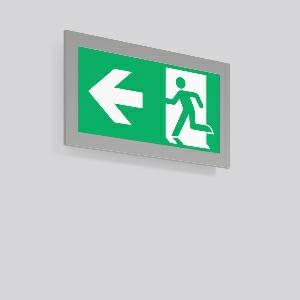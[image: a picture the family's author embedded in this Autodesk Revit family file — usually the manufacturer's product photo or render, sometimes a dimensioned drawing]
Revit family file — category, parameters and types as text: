
# Revit family: tenuo_671923_004_89_73a6
name_source: partatom
category: Lighting Fixtures
units: mm (PartAtom-declared; Revit-internal decimal feet)

## family parameters
Cut with Voids When Loaded = No
Host = Face
Light Source = No
Part Type = Normal
Room Calculation Point = No
Round Connector Dimension = Use Diameter
Shared = No

## types (1)
- TENUO
    Apparent Load = 0 VA
    Default Elevation = 1800 mm
    Description = Series: TENUO
Luminaire for escape route identification. Housing: anodised aluminium, silver. Display panel: patented MicroLens technology and legend on one side. Driver integrated. Suitable for connection to central battery systems. With AC Control monitoring module for LUXIFAIR central battery units. Please indicate legend number when placing your order! 
Colour: silver, matt (approx. RAL 9006)
Length: 350 mm
Width: 33 mm
Height: 200 mm
Weight: 1.52 kg
Operating mode: maintained power mode
Viewing Distance: 30 m
Lamp: LED
Socket: without socket
Colour temperature: 5700K
Colour rendering index (CRI): 80
System power: 4.8 W
System power, emergency: 4.8 W
Control gear: Regulated power supply
Protection class: I
Type of protection: IP 40
    Height = 200 mm  [stored 0.656168 ft]
    Lamp = 0 x
    Length = 350 mm
    Luminous efficacy = 0 lm/W
    Manufacturer = RZB
    ModVariant = No
    Model = 671923.004.89
    Mounting Place = Wall
    Mounting Type = Surface mounted
    Number of Poles = 1
    OnlyDefault = Yes
    Power Factor = 1
    Product Name = TENUO
    Product group = Surface mounted Wall luminaires
    ProductGroupID = 2001
    Protection Class = Protection class I
    Protection Degree = IP 40
    RLX_Detail_Level = 1
    RLX_Emergency_Light_Flux = 0 lm
    RLX_Emergency_Type = 0
    RLX_Emergency_Type_DB = No
    RlxData = <blob elided: 28057 chars, md5=08847f18>
    Standby Power = 0 W
    System Light Flux = 0 lm
    System Power = 0 W
    Type Comments = ALEA SPOT
    Type Image = 671923.004.jpg
    URL = http://relux.com
    VarID = ---
    Voltage = 230 V
    Voltage Range = 220-240 V
    Weight = 0.00 kg
    Width = 33 mm

note: [stored X ft] marks values corroborated as IEEE doubles in the binary element streams (Revit-internal decimal feet)

## geometry (parser evidence)
native form markers: Blend x4, Sweep x10
no freeform markers — native parametric forms only
